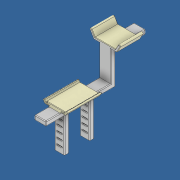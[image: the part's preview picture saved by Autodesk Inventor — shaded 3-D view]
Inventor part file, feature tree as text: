
AUTODESK INVENTOR PART (.ipt)
format: ipt  version: 2021 (Build 250183000, 183)  size: 549,888 bytes
history: native  units: mm
features: fillet x11, extrude x8, sketch x8, plane x2, chamfer x1
ambient origin geometry x8: Origin, YZ Plane, XZ Plane, XY Plane, X Axis, Y Axis, Z Axis, Center Point
bodies: Solid1 (feature_tree)
feature tree (30):
  extrude  "Extrusion1"  Depth=300.0mm
  extrude  "Extrusion2"  Depth=130.0mm
  extrude  "Extrusion3"  Depth=20.0mm TaperAngle=0.0deg
  plane  "Work Plane1"
  extrude  "Extrusion5"  Depth=150.0mm
  fillet  "Fillet1"  Radius=20.0mm
  fillet  "Fillet2"  [1 undecoded]
  fillet  "Fillet3"  Radius=140.0mm
  plane  "Work Plane2"
  extrude  "Extrusion6"  Depth=20.0mm
  fillet  "Fillet4"  Radius=20.0mm
  fillet  "Fillet6"  Radius=25.0mm
  fillet  "Fillet7"  Radius=10.0mm
  chamfer  "Chamfer1"  Distance=11.517511mm
  fillet  "Fillet8"  Radius=100.0mm
  fillet  "Fillet9"  Radius=5.0mm
  fillet  "Fillet10"  Radius=2.0mm
  fillet  "Fillet11"  Radius=2.0mm
  extrude  "Extrusion8"  Depth=4.0mm
  extrude  "Extrusion9"  Depth=4.0mm
  extrude  "Extrusion10"  Depth=10.0mm
  fillet  "Fillet12"  Radius=10.0mm
  sketch  "Sketch1"  dims[d0=50.0mm d1=300.0mm]
  sketch  "Sketch2"  dims[d2=20.0mm d3=0.0mm d4=130.0mm]
  sketch  "Sketch3"  dims[d5=50.0mm d6=20.0mm d7=0.0mm]
  sketch  "Sketch5"  dims[d8=50.0mm d9=150.0mm d10=20.0mm d11=0.0mm d18=-50.0mm d19=140.0mm]
  sketch  "Sketch6"  dims[d20=35.0mm d21=20.0mm d22=20.0mm d23=20.0mm d24=25.0mm d25=10.0mm]
  sketch  "Sketch8"  dims[d26=10.0mm]
  sketch  "Sketch9"  dims[d27=10.0mm]
  sketch  "Sketch10"  dims[d28=11.517511mm d29=11.517511mm d30=100.0mm d31=0.0mm d32=5.0mm d33=2.0mm d34=2.0mm d35=65.0mm d36=90.0mm d37=10.0mm d38=10.0mm d39=15.0mm d40=0.0mm d41=20.0mm d42=7.5mm d43=7.5mm d44=7.5mm d45=15.0mm d46=150.0mm d47=0.0mm d48=3.5mm d50=3.0mm d51=3.0mm d52=4.0mm d53=2.0mm d54=45.0deg d55=4.0mm d56=3.0mm d57=3.0mm d58=3.0mm d64=20.0mm d65=20.0mm d66=88.986mm d67=43.856207mm d68=43.856207mm d69=150.0mm d70=0.0mm d71=4.0mm d72=4.0mm d73=4.0mm d74=4.0mm d75=4.0mm d76=4.0mm d77=4.0mm d78=4.0mm d79=3.0mm d80=20.0mm d81=21.928mm d82=25.0mm d83=10.0mm d84=0.0mm d85=3.0mm d86=20.0mm d87=21.928mm d89=50.0mm d90=20.0mm d91=3.0mm d92=21.928mm d95=75.0mm d98=3.0mm d99=20.0mm d100=21.928mm d101=100.0mm d102=21.928mm d103=20.0mm d104=3.0mm d105=125.0mm d106=100.0mm d107=0.0mm d108=4.0mm d109=4.0mm]
note: 1 required parameter value undecoded (feature->parameter linkage not recoverable at this tier; creation-order binding heuristic only, values carry confidence <= 0.55)
